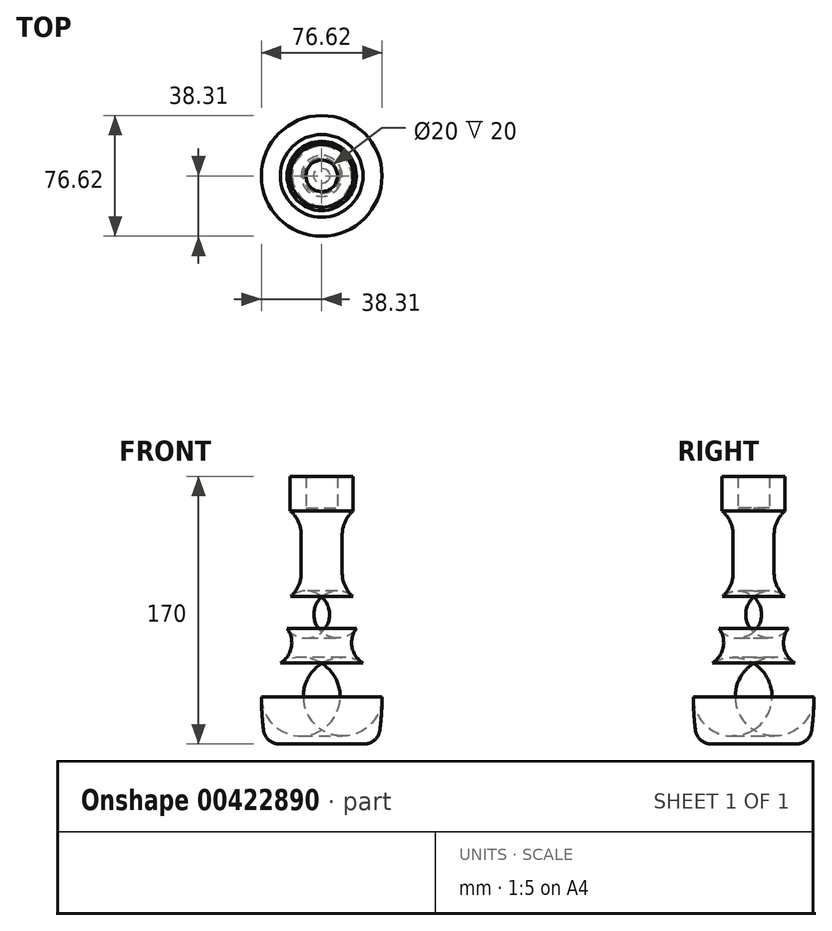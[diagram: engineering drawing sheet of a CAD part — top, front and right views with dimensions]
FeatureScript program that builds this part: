
annotation { "Feature Type Name" : "Feature", "Feature Type Description" : "" }
export const myFeature = defineFeature(function(context is Context, id is Id, definition is map)
    precondition{}
    {
        {
            var Q0;
            Q0=qCreatedBy(makeId("Front.planeOp"),FACE);
            var sketch = newSketch(context, id + "F0", { "sketchPlane" : qUnion([Q0])});
            skLineSegment(sketch, "E0", {"start": v(0, 0) * mm, "end": v(0, 182.78) * mm, "construction": true});
            skLineSegment(sketch, "E1", {"start": v(0, 0) * mm, "end": v(0, 150) * mm});
            skLineSegment(sketch, "E2", {"start": v(10, 170) * mm, "end": v(20, 170) * mm});
            skLineSegment(sketch, "E3", {"start": v(0, 0) * mm, "end": v(27, 0) * mm});
            skLineSegment(sketch, "E4", {"start": v(20, 170) * mm, "end": v(20, 148) * mm});
            skLineSegment(sketch, "E5", {"start": v(13, 132.8) * mm, "end": v(13, 108.62) * mm});
            skArc(sketch, "E6", {"start": v(27, 0) * mm, "mid": v(33.6, 2.48) * mm, "end": v(36.91, 8.7) * mm});
            skArc(sketch, "E7", {"start": v(38.31, 30) * mm, "mid": v(35.08, 42.28) * mm, "end": v(26.24, 51.4) * mm});
            skArc(sketch, "E8", {"start": v(26.24, 51.4) * mm, "mid": v(19.28, 61.37) * mm, "end": v(22, 73.23) * mm});
            skArc(sketch, "E9", {"start": v(22, 73.23) * mm, "mid": v(24.92, 83.8) * mm, "end": v(19.86, 93.54) * mm});
            skArc(sketch, "E10", {"start": v(19.86, 93.54) * mm, "mid": v(14.8, 100.33) * mm, "end": v(13, 108.62) * mm});
            skArc(sketch, "E11", {"start": v(13, 132.8) * mm, "mid": v(14.83, 141.17) * mm, "end": v(20, 148) * mm});
            skArc(sketch, "E12", {"start": v(36.91, 8.7) * mm, "mid": v(37.96, 19.32) * mm, "end": v(38.31, 30) * mm});
            skLineSegment(sketch, "E13", {"start": v(10, 170) * mm, "end": v(10, 150) * mm});
            skLineSegment(sketch, "E14", {"start": v(10, 150) * mm, "end": v(0, 150) * mm});
            skPoint(sketch, "E15.orphan", {"position": v(0, 170) * mm});
            skSolve(sketch);
        }
        {
            var Q0;
            Q0=makeQuery(id+"F0.imprint","IMPRINT",FACE,{"disambiguationData":[TD([[makeQuery(id+"F0.imprint","IMPRINT",EDGE,{"derivedFrom":sQuery(id+"F0.wireOp",EDGE,"E1")}),-1.0]])]});
            var Q1;
            Q1=sQuery(id+"F0.wireOp",EDGE,"E0");
            revolve(context, id + "F1", {"entities" : qUnion([Q0]), "axis" : qUnion([Q1]), "revolveType" : RevolveType.FULL});
        }
    });
